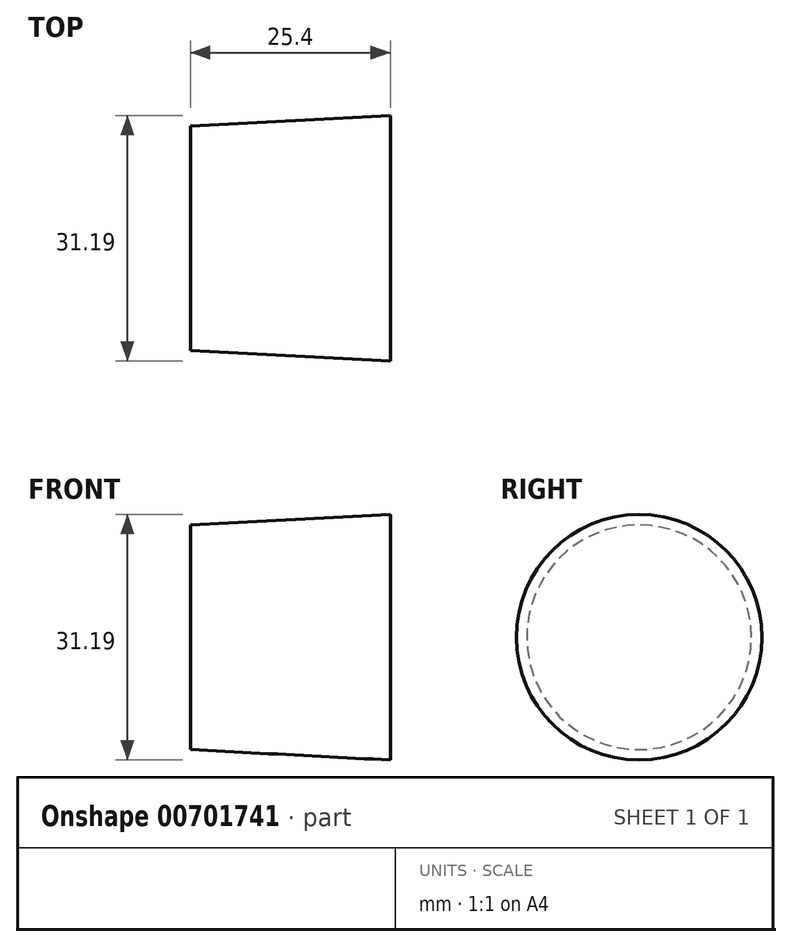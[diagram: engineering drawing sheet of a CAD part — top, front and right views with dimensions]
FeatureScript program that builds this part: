
annotation { "Feature Type Name" : "Feature", "Feature Type Description" : "" }
export const myFeature = defineFeature(function(context is Context, id is Id, definition is map)
    precondition{}
    {
        {
            var Q0;
            Q0=qCreatedBy(makeId("Right.planeOp"),FACE);
            var sketch = newSketch(context, id + "F0", { "sketchPlane" : qUnion([Q0])});
            skCircle(sketch, "E0", {"center": v(-38.41, 18.27) * mm, "radius": 14.27 * mm});
            skSolve(sketch);
        }
        {
            var Q0;
            Q0=makeQuery(id+"F0.imprint","IMPRINT",FACE,{"disambiguationData":[TD([[makeQuery(id+"F0.imprint","IMPRINT",EDGE,{"derivedFrom":sQuery(id+"F0.wireOp",EDGE,"E0")}),1.0]])]});
            extrude(context, id + "F1", {"entities" : qUnion([Q0]), "depth" : 25.4 * mm, "offsetDistance" : 25.4 * mm, "hasDraft" : true, "draftAngle" : 3 * degree});
        }
    });
